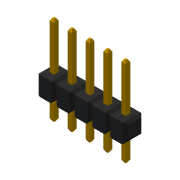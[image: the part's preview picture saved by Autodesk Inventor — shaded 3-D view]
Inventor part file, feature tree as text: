
AUTODESK INVENTOR PART (.ipt)
format: ipt  version: 2016 (Build 200138000, 138)  size: 369,152 bytes
history: native  units: mm
features: other x8, sketch x3, extrude x2, projected_geometry x1
ambient origin geometry x8: Origin, YZ Plane, XZ Plane, XY Plane, X Axis, Y Axis, Z Axis, Center Point
bodies: Solid1 (feature_tree), Solid2 (feature_tree), Solid3 (feature_tree), Solid4 (feature_tree), Solid5 (feature_tree)
feature tree (14):
  other  "Repaired Geometry1"
  extrude  "Extrusion1"  Depth=0.01mm TaperAngle=0.0deg
  extrude  "Extrusion2"  [1 undecoded]
  sketch  "3D Sketch1"
  sketch  "Sketch1"  dims[d0=0.01mm d1=0.0mm d2=0.01mm d3=0.0mm]
  sketch  "Sketch2"
  projected_geometry  "Projected Loop1"
  other  "brep_1"
  other  "brep_2"
  other  "brep_3"
  other  "brep_4"
  other  "brep_5"
  other  "Composite1"
  other  "Srf1"
note: 1 required parameter value undecoded (feature->parameter linkage not recoverable at this tier; creation-order binding heuristic only, values carry confidence <= 0.55)
